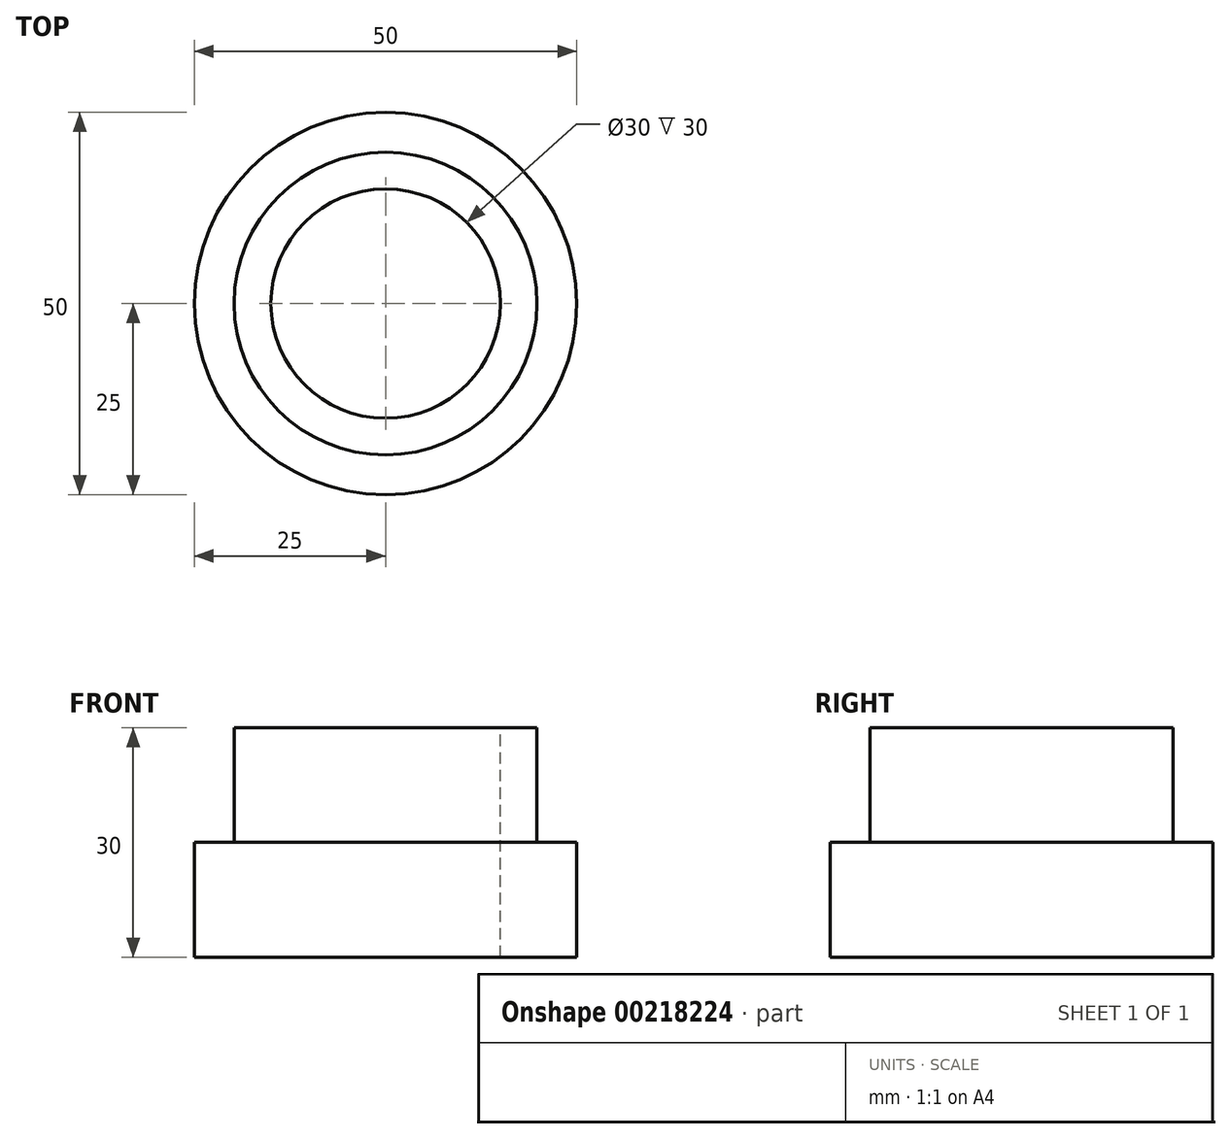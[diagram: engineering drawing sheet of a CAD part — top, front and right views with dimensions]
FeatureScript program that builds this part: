
annotation { "Feature Type Name" : "Feature", "Feature Type Description" : "" }
export const myFeature = defineFeature(function(context is Context, id is Id, definition is map)
    precondition{}
    {
        {
            var Q0;
            Q0=qCreatedBy(makeId("Front.planeOp"),FACE);
            var sketch = newSketch(context, id + "F0", { "sketchPlane" : qUnion([Q0])});
            skLineSegment(sketch, "E0", {"start": v(0, 56.95) * mm, "end": v(0, -65.66) * mm, "construction": true});
            skLineSegment(sketch, "E1.bottom", {"start": v(25, -15) * mm, "end": v(-25, -15) * mm});
            skLineSegment(sketch, "E1.top", {"start": v(25, 15) * mm, "end": v(-25, 15) * mm});
            skLineSegment(sketch, "E1.left", {"start": v(25, -15) * mm, "end": v(25, 15) * mm});
            skLineSegment(sketch, "E1.right", {"start": v(-25, -15) * mm, "end": v(-25, 15) * mm});
            skPoint(sketch, "E1.middle", {"position": v(0, 0) * mm});
            skLineSegment(sketch, "E2", {"start": v(-15, 15) * mm, "end": v(-15, -15) * mm});
            skLineSegment(sketch, "E3.MirrorCS", {"start": v(15, 15) * mm, "end": v(15, -15) * mm});
            skLineSegment(sketch, "E4", {"start": v(-25, 0) * mm, "end": v(-15, 0) * mm});
            skLineSegment(sketch, "E5", {"start": v(-19.8, 15) * mm, "end": v(-19.8, 0) * mm});
            skLineSegment(sketch, "E6.MirrorCS", {"start": v(25, 0) * mm, "end": v(15, 0) * mm});
            skLineSegment(sketch, "E7.MirrorCS", {"start": v(19.8, 15) * mm, "end": v(19.8, 0) * mm});
            skSolve(sketch);
        }
        {
            var Q0;
            {var subQ1=sQuery(id+"F0.wireOp",EDGE,"E1.bottom");var subQ6=sQuery(id+"F0.wireOp",EDGE,"E1.right");var subQ7=makeQuery(id+"F0.imprint","INTERSECT",VERTEX,{"derivedFrom":[subQ1,subQ6]});Q0=makeQuery(id+"F0.imprint","IMPRINT",FACE,{"disambiguationData":[TD([[makeQuery(id+"F0.imprint","IMPRINT",EDGE,{"disambiguationData":[TD([[subQ7,1.0]])],"derivedFrom":subQ1}),-1.0]])]});}
            var Q1;
            {var subQ3=sQuery(id+"F0.wireOp",EDGE,"E5");Q1=makeQuery(id+"F0.imprint","IMPRINT",FACE,{"disambiguationData":[TD([[makeQuery(id+"F0.imprint","IMPRINT",EDGE,{"derivedFrom":subQ3}),1.0]])]});}
            var Q2;
            Q2=sQuery(id+"F0.wireOp",EDGE,"E0");
            revolve(context, id + "F1", {"entities" : qUnion([Q0, Q1]), "axis" : qUnion([Q2]), "revolveType" : RevolveType.FULL});
        }
    });
